# Revit family: Gira_117100
name_source: partatom
category: Electrical Fixtures
revit_build: Autodesk Revit 2017 (Build: 20160225_1515(x64)
units: mm (PartAtom-declared; Revit-internal decimal feet)

## family parameters
Cut with Voids When Loaded = No
Host = Face
Maintain Annotation Orientation = Yes
Part Type = Normal
Room Calculation Point = No
Round Connector Dimension = Use Diameter
Shared = No

## types (1)
- LED-Signalleuchte RT / GN System 55
    Available = Yes
    Category = Überwachbare LED Signalleuchte
    Data sheet (1) = https://katalog.gira.de
    Default Elevation = 1219 mm
    GTIN = 4010337049289
    HAN = 117100
    HeinzeBIM = https://bimportal.heinze.de
    Kalottenfarbe = sonstige
    Manufacturer URL = https://www.gira.de
    Model = Sys55_Komplettgerät_Schalten und Tasten
    Name = LED-Signalleuchte RT / GN System 55
    Nennspannung = 230 Volt
    Region = DE
    Schutzart (IP) = IP20
    Stromart = Ac (*en-EN)
    URL = http://katalog.gira.de

## geometry (parser evidence)
native form markers: Blend x2, Sweep x8
no freeform markers — native parametric forms only
